# Revit family: equip-water-cooler-hlsy-tylr-hacv2-hthb
name_source: partatom
category: Plumbing Fixtures
units: mm (PartAtom-declared; Revit-internal decimal feet)

## family parameters
Always vertical = Yes
Cut with Voids When Loaded = No
OmniClass Number = 23.45.00.00
OmniClass Title = Sanitary, Laundry, and Cleaning Equipment
Part Type = Normal
Room Calculation Point = No
Round Connector Dimension = Use Radius
Shared = No
Work Plane-Based = No

## types (1)
- equip-water-cooler-hlsy-tylr-hacv2-hthb
    Apparent Load Phase 1 = 0 VA
    Basin Material = Metal - Steel - Stainless - Chrome
    Button Material = Plastic - Brown
    CW Connection = Yes
    Cooler Bottom = 1' - 0 3/8"
    Cooler Depth = 1' - 6 5/8"
    Cooler Height = 1' - 8 5/8"
    Cooler Rear Panel Depth = 0' - 6 27/32"
    Cooler Width = 1' - 6 1/16"
    Description = Mechanical pushbar actuated water cooler
    Dispenser Depth = 0' - 8"
    Dispenser Height = 2' - 3 1/16"
    Glass Filter = -
    HW Connection = No
    Manufacturer = Halsey Taylor
    Model = HTHB-HAC8WF
    Numbe of Poles = 1
    Orifice Height = 2' - 9"
    Orifice to Rim = 0' - 1 13/16"
    Panel Material = Metal - Steel - Stainless - Color 1
    Power Factor = 1
    Rim Height = 2' - 7 3/16"
    Rim to Dispenser = 0' - 4 1/8"
    Sanitary Service Radius = 0' - 0 5/8"
    Specification URL = http://www.halseytaylor.com
    Type = Single
    URL = http://www.halseytaylor.com
    Vent Connection = No
    Version = 1.0.0.0
    Voltage = 0 V
    Waste Connection = Yes
    Water Service Flow = 0 GPM
    Water Service Size Radius = 0' - 0 1/4"

## geometry (parser evidence)
native form markers: Sweep x13
no freeform markers — native parametric forms only
